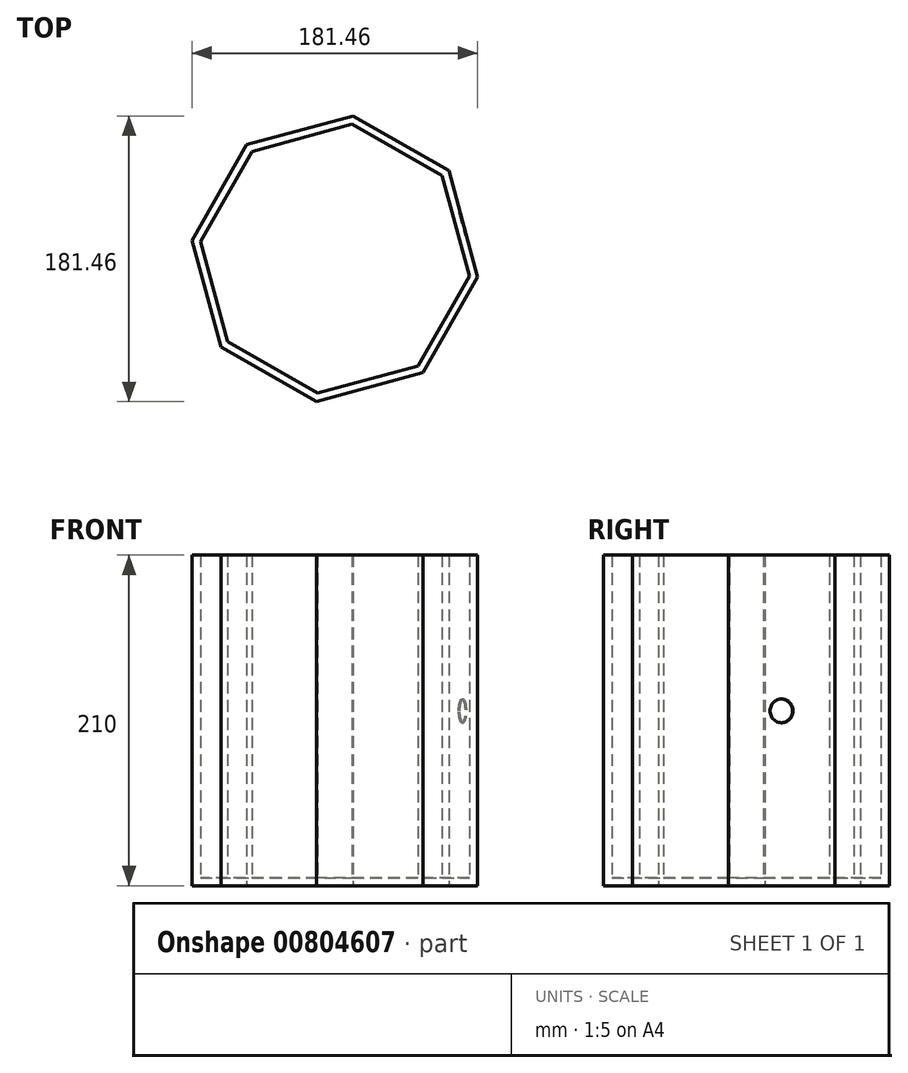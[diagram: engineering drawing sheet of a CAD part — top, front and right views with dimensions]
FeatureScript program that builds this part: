
annotation { "Feature Type Name" : "Feature", "Feature Type Description" : "" }
export const myFeature = defineFeature(function(context is Context, id is Id, definition is map)
    precondition{}
    {
        {
            var Q0;
            Q0=qCreatedBy(makeId("Top.planeOp"),FACE);
            var sketch = newSketch(context, id + "F0", { "sketchPlane" : qUnion([Q0])});
            skCircle(sketch, "E0.cCircle", {"center": v(0, 0) * mm, "radius": 84.5 * mm, "construction": true});
            skLineSegment(sketch, "E0.0", {"start": v(90.73, -11.57) * mm, "end": v(55.97, -72.33) * mm});
            skLineSegment(sketch, "E0.1", {"start": v(55.97, -72.33) * mm, "end": v(-11.57, -90.73) * mm});
            skLineSegment(sketch, "E0.2", {"start": v(-11.57, -90.73) * mm, "end": v(-72.33, -55.97) * mm});
            skLineSegment(sketch, "E0.3", {"start": v(-72.33, -55.97) * mm, "end": v(-90.73, 11.57) * mm});
            skLineSegment(sketch, "E0.4", {"start": v(-90.73, 11.57) * mm, "end": v(-55.97, 72.33) * mm});
            skLineSegment(sketch, "E0.5", {"start": v(-55.97, 72.33) * mm, "end": v(11.57, 90.73) * mm});
            skLineSegment(sketch, "E0.6", {"start": v(11.57, 90.73) * mm, "end": v(72.33, 55.97) * mm});
            skLineSegment(sketch, "E0.7", {"start": v(72.33, 55.97) * mm, "end": v(90.73, -11.57) * mm});
            skPoint(sketch, "E0.0.midPoint", {"position": v(73.35, -41.95) * mm});
            skSolve(sketch);
        }
        {
            var Q0;
            Q0 = qSketchRegion(id + "F0", true);
            extrude(context, id + "F1", {"entities" : qUnion([Q0]), "depth" : 210 * mm, "offsetDistance" : 25.4 * mm});
        }
        {
            var Q0;
            Q0=makeQuery(id+"F1.opExtrude","CAP_FACE",FACE,{"disambiguationData":[OSD([sQuery(id+"F0.wireOp",EDGE,"E0.0"),sQuery(id+"F0.wireOp",EDGE,"E0.1"),sQuery(id+"F0.wireOp",EDGE,"E0.2"),sQuery(id+"F0.wireOp",EDGE,"E0.3"),sQuery(id+"F0.wireOp",EDGE,"E0.4"),sQuery(id+"F0.wireOp",EDGE,"E0.5"),sQuery(id+"F0.wireOp",EDGE,"E0.6"),sQuery(id+"F0.wireOp",EDGE,"E0.7")])],"isStart":false});
            shell(context, id + "F2", {"entities" : qUnion([Q0]), "thickness" : 5 * mm});
        }
        {
            var Q0;
            Q0=makeQuery(id+"F1.opExtrude","SWEPT_FACE",FACE,{"disambiguationData":[OSD([sQuery(id+"F0.wireOp",EDGE,"E0.7")])]});
            var sketch = newSketch(context, id + "F3", { "sketchPlane" : qUnion([Q0])});
            skCircle(sketch, "E1", {"center": v(0, 111) * mm, "radius": 7.55 * mm});
            skSolve(sketch);
        }
        {
            var Q0;
            Q0 = qSketchRegion(id + "F3", true);
            extrude(context, id + "F4", {"entities" : qUnion([Q0]), "operationType" : NewBodyOperationType.REMOVE, "oppositeDirection" : true, "depth" : 1 * mm, "offsetDistance" : 25.4 * mm});
        }
    });
